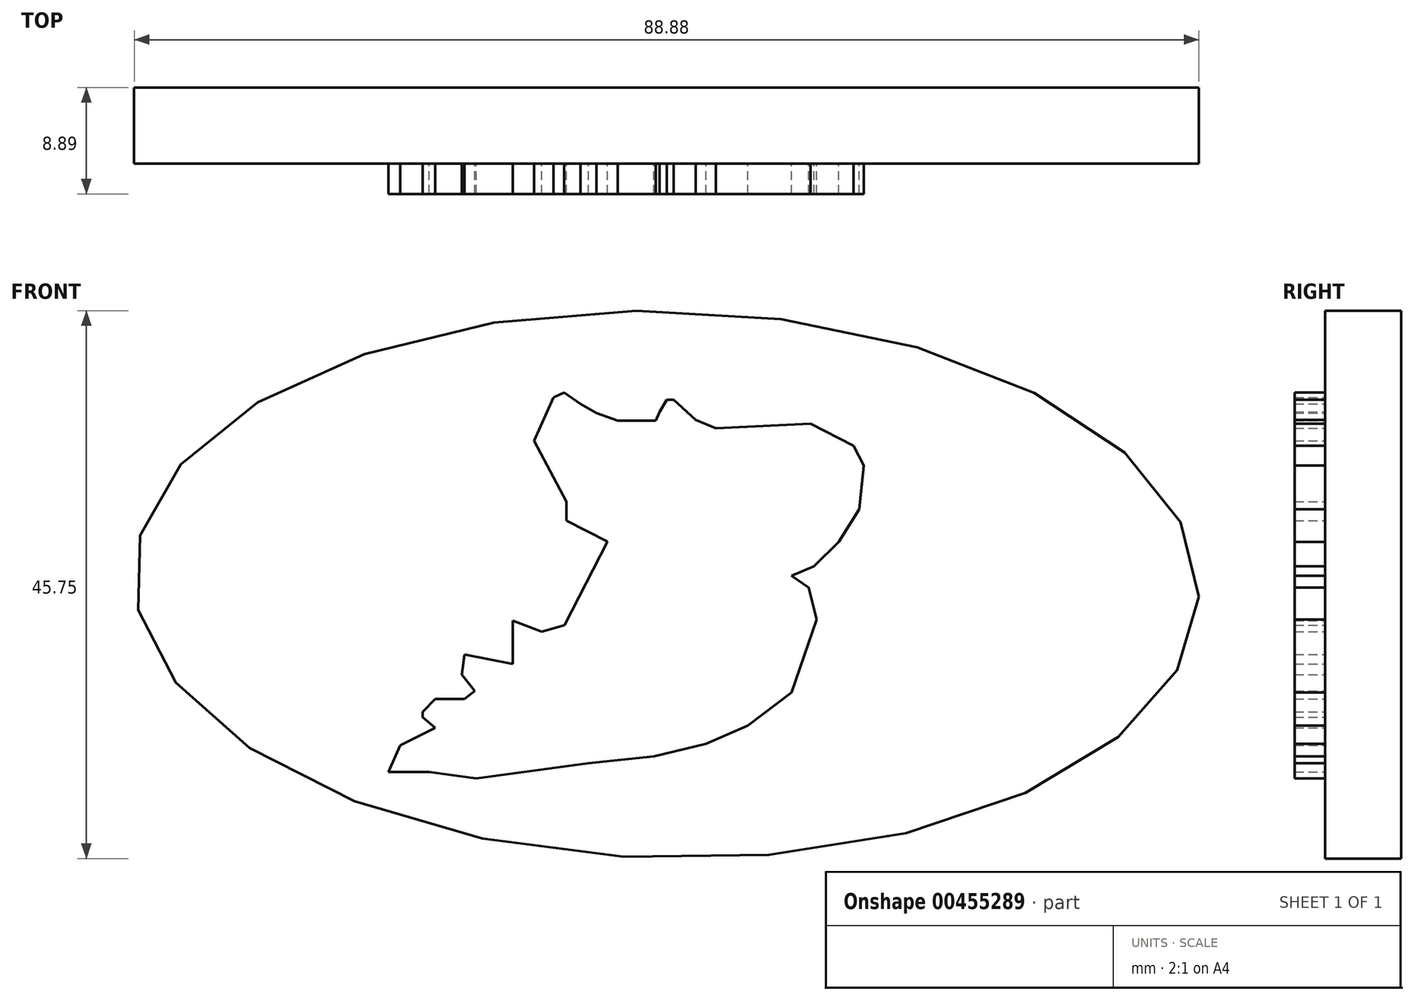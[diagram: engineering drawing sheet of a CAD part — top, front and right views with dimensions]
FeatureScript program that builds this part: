
annotation { "Feature Type Name" : "Feature", "Feature Type Description" : "" }
export const myFeature = defineFeature(function(context is Context, id is Id, definition is map)
    precondition{}
    {
        {
            var Q0;
            Q0=qCreatedBy(makeId("Front.planeOp"),FACE);
            var sketch = newSketch(context, id + "F0", { "sketchPlane" : qUnion([Q0])});
            skEllipse(sketch, "E0", {"center": v(-62.52, 45.96) * mm, "majorRadius": 44.45 * mm, "minorRadius": 22.86 * mm, "majorAxis": v(1, -0.02)});
            skSolve(sketch);
        }
        {
            var Q0;
            Q0 = qSketchRegion(id + "F0", true);
            extrude(context, id + "F1", {"entities" : qUnion([Q0]), "depth" : 6.35 * mm});
        }
        {
            var Q0;
            Q0=makeQuery(id+"F1.opExtrude","CAP_FACE",FACE,{"disambiguationData":[OSD([sQuery(id+"F0.wireOp",EDGE,"E0")])],"isStart":false});
            var sketch = newSketch(context, id + "F2", { "sketchPlane" : qUnion([Q0])});
            skLineSegment(sketch, "E1", {"start": v(-50.51, 59.41) * mm, "end": v(-58.4, 59.01) * mm});
            skLineSegment(sketch, "E2", {"start": v(-58.4, 59.01) * mm, "end": v(-60.07, 59.72) * mm});
            skLineSegment(sketch, "E3", {"start": v(-60.07, 59.72) * mm, "end": v(-61.94, 61.4) * mm});
            skLineSegment(sketch, "E4", {"start": v(-61.94, 61.4) * mm, "end": v(-62.49, 61.4) * mm});
            skLineSegment(sketch, "E5", {"start": v(-62.49, 61.4) * mm, "end": v(-63.11, 60.37) * mm});
            skLineSegment(sketch, "E6", {"start": v(-63.11, 60.37) * mm, "end": v(-63.41, 59.64) * mm});
            skLineSegment(sketch, "E7", {"start": v(-64.37, 59.64) * mm, "end": v(-66.58, 59.64) * mm});
            skLineSegment(sketch, "E8", {"start": v(-66.58, 59.64) * mm, "end": v(-68.36, 60.3) * mm});
            skLineSegment(sketch, "E9", {"start": v(-68.36, 60.3) * mm, "end": v(-69.72, 61.06) * mm});
            skLineSegment(sketch, "E10", {"start": v(-63.41, 59.64) * mm, "end": v(-64.37, 59.64) * mm});
            skLineSegment(sketch, "E11", {"start": v(-69.72, 61.06) * mm, "end": v(-71.52, 62.33) * mm});
            skLineSegment(sketch, "E12", {"start": v(-71.07, 62.02) * mm, "end": v(-71.96, 61.6) * mm});
            skLineSegment(sketch, "E13", {"start": v(-71.96, 61.6) * mm, "end": v(-73.56, 57.96) * mm});
            skLineSegment(sketch, "E14", {"start": v(-71.02, 53.17) * mm, "end": v(-70.87, 52.88) * mm});
            skLineSegment(sketch, "E15", {"start": v(-70.87, 52.88) * mm, "end": v(-70.87, 51.31) * mm});
            skLineSegment(sketch, "E16", {"start": v(-70.87, 51.31) * mm, "end": v(-67.46, 49.57) * mm});
            skLineSegment(sketch, "E17", {"start": v(-67.46, 49.57) * mm, "end": v(-71.04, 42.56) * mm});
            skLineSegment(sketch, "E18", {"start": v(-50.51, 59.41) * mm, "end": v(-46.9, 57.56) * mm});
            skLineSegment(sketch, "E19", {"start": v(-79.38, 40.14) * mm, "end": v(-79.6, 38.44) * mm});
            skLineSegment(sketch, "E20", {"start": v(-79.6, 38.44) * mm, "end": v(-78.53, 37.09) * mm});
            skLineSegment(sketch, "E21", {"start": v(-79.39, 36.42) * mm, "end": v(-81.82, 36.42) * mm});
            skLineSegment(sketch, "E22", {"start": v(-81.82, 36.42) * mm, "end": v(-82.89, 35.33) * mm});
            skLineSegment(sketch, "E23", {"start": v(-82.89, 34.88) * mm, "end": v(-81.82, 33.99) * mm});
            skLineSegment(sketch, "E24", {"start": v(-81.82, 33.99) * mm, "end": v(-84.74, 32.55) * mm});
            skLineSegment(sketch, "E25", {"start": v(-46.05, 52.9) * mm, "end": v(-48.14, 49.53) * mm});
            skLineSegment(sketch, "E26", {"start": v(-48.14, 49.53) * mm, "end": v(-50.22, 47.5) * mm});
            skLineSegment(sketch, "E27", {"start": v(-50.22, 47.5) * mm, "end": v(-52.08, 46.7) * mm});
            skLineSegment(sketch, "E28", {"start": v(-52.08, 46.7) * mm, "end": v(-50.66, 45.72) * mm});
            skLineSegment(sketch, "E29", {"start": v(-50.66, 45.72) * mm, "end": v(-50, 43.04) * mm});
            skLineSegment(sketch, "E30", {"start": v(-50, 43.04) * mm, "end": v(-52.08, 36.94) * mm});
            skLineSegment(sketch, "E31", {"start": v(-52.08, 36.94) * mm, "end": v(-55.73, 34.19) * mm});
            skLineSegment(sketch, "E32", {"start": v(-55.73, 34.19) * mm, "end": v(-59.22, 32.68) * mm});
            skLineSegment(sketch, "E33", {"start": v(-59.22, 32.68) * mm, "end": v(-63.57, 31.61) * mm});
            skLineSegment(sketch, "E34", {"start": v(-63.57, 31.61) * mm, "end": v(-69.03, 31.04) * mm});
            skLineSegment(sketch, "E35", {"start": v(-69.03, 31.04) * mm, "end": v(-75.43, 30.19) * mm});
            skLineSegment(sketch, "E36", {"start": v(-75.43, 30.19) * mm, "end": v(-78.4, 29.79) * mm});
            skLineSegment(sketch, "E37", {"start": v(-78.4, 29.79) * mm, "end": v(-82.35, 30.3) * mm});
            skPoint(sketch, "E37.endSnap0", {"position": v(-82.35, 34.44) * mm});
            skLineSegment(sketch, "E38", {"start": v(-82.35, 30.3) * mm, "end": v(-85.73, 30.3) * mm});
            skLineSegment(sketch, "E39", {"start": v(-46.9, 57.56) * mm, "end": v(-46.06, 55.9) * mm});
            skLineSegment(sketch, "E40", {"start": v(-46.06, 55.9) * mm, "end": v(-46.44, 52.27) * mm});
            skLineSegment(sketch, "E41", {"start": v(-78.53, 37.09) * mm, "end": v(-79.39, 36.42) * mm});
            skPoint(sketch, "E42.end.orphan", {"position": v(-75.34, 40.14) * mm});
            skLineSegment(sketch, "E43", {"start": v(-75.34, 40.14) * mm, "end": v(-75.34, 39.34) * mm});
            skLineSegment(sketch, "E44", {"start": v(-71.04, 42.56) * mm, "end": v(-72.94, 42.02) * mm});
            skLineSegment(sketch, "E45", {"start": v(-72.94, 42.02) * mm, "end": v(-75.34, 42.96) * mm});
            skLineSegment(sketch, "E46", {"start": v(-75.34, 39.34) * mm, "end": v(-79.38, 40.14) * mm});
            skLineSegment(sketch, "E47", {"start": v(-82.89, 35.33) * mm, "end": v(-82.89, 34.88) * mm});
            skLineSegment(sketch, "E48", {"start": v(-75.34, 42.96) * mm, "end": v(-75.34, 40.14) * mm});
            skPoint(sketch, "E49.end.orphan", {"position": v(-71.52, 64.68) * mm});
            skLineSegment(sketch, "E50.trimOffspring", {"start": v(-84.74, 32.55) * mm, "end": v(-85.73, 30.3) * mm});
            skLineSegment(sketch, "E51", {"start": v(-70.87, 52.88) * mm, "end": v(-72.26, 55.5) * mm});
            skLineSegment(sketch, "E52", {"start": v(-72.26, 55.5) * mm, "end": v(-73.56, 57.96) * mm});
            skPoint(sketch, "E53.orphan", {"position": v(-70.87, 56.24) * mm});
            skSolve(sketch);
        }
        {
            var Q0;
            Q0=makeQuery(id+"F2.imprint","IMPRINT",FACE,{"disambiguationData":[TD([[makeQuery(id+"F2.imprint","IMPRINT",EDGE,{"derivedFrom":sQuery(id+"F2.wireOp",EDGE,"E1")}),1.0]])]});
            extrude(context, id + "F3", {"entities" : qUnion([Q0]), "operationType" : NewBodyOperationType.ADD, "depth" : 2.54 * mm});
        }
    });
